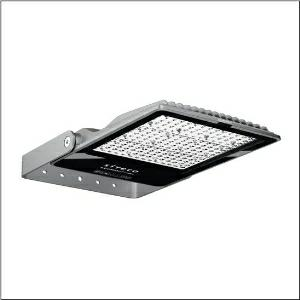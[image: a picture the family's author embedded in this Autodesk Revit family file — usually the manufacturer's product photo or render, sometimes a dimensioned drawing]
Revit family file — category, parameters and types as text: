
# Revit family: sicompact_31_midi___pl32_5xa7581e1k23_2b07
name_source: partatom
category: Lighting Fixtures
units: mm (PartAtom-declared; Revit-internal decimal feet)

## family parameters
Cut with Voids When Loaded = No
Host = Face
Light Source = No
Part Type = Normal
Room Calculation Point = No
Round Connector Dimension = Use Diameter
Shared = No

## types (1)
- SiCompact 31 midi  PL32 (1 x LED, 37000 lm, 250 W, 3000K)
    Apparent Load = 250 VA
    CIE Flux Codes = 32 69 98 100 100
    Color Rendering = 70
    Color Temperature = 3000K
    Default Elevation = 1800 mm
    Description = SiCompact 31 midi, floodlight, primary light control with lens, of plastic, of toughened safety glass, transparent, light distribution: PL32, light emission: direct distribution, primary light characteristic: asymmetric, installation type: surface-mounted, LED, High Power LED, rated luminous flux: 37.000lm, luminous efficacy: 148lm/W, light colour: 730, colour temperature: 3000K, control gear: ON/OFF, with cable, 3x 1.5mm², mains connection: 220..240V, AC, 50/60Hz, connection cable pre-assembled, cable length: 2m, rated input power: 250W, of diecast aluminium, specular, metallic grey (RAL 9006), length: 560mm, width: 330mm, height: 62mm, bracket, of sheet steel, coated, metallic grey (RAL 9006), ON/OFF, protection rating (complete): IP66, insulation class (complete): insulation class I (protective earthing), certification: CE, ENEC, impact resistance: IK08, permissible operating ambient temperature: -40..+45°C, packaging unit: 1 piece

Light Distribution: PL32
    Height = 62 mm  [stored 0.203412 ft]
    Lamp = 1 x LED
    Lamp Light Flux = 37000 lm
    Lamp Power = 250 W
    Lamp count = 1
    Length = 560 mm
    Luminous efficacy = 148 lm/W
    Manufacturer = Siteco
    ModVariant = No
    Model = 5XA7581E1K23
    Mounting Place = Wall
    Mounting Type = Surface mounted
    Number of Poles = 1
    OnlyDefault = Yes
    Power Factor = 1
    Product Name = SiCompact 31 midi | PL32
    Product group = floodlight | wall mounted
    ProductGroupID = 2002
    Protection Class = Protection class I
    Protection Degree = IP 66
    RLX_Detail_Level = 1
    RLX_Emergency_Light_Flux = 0 lm
    RLX_Emergency_Type = 0
    RLX_Emergency_Type_DB = No
    RlxData = <blob elided: 97977 chars, md5=3f6681a1>
    Socket = socket
    Standby Power = 0 W
    System Light Flux = 37000 lm
    System Power = 250 W
    Type Comments = Product without accessories
    Type Image = l_1006415.jpg
    URL = http://relux.com
    VarID = ---
    Voltage = 0 V
    Weight = 0.00 kg
    Width = 333 mm

note: [stored X ft] marks values corroborated as IEEE doubles in the binary element streams (Revit-internal decimal feet)

## geometry (parser evidence)
native form markers: Blend x4, Sweep x14
no freeform markers — native parametric forms only
